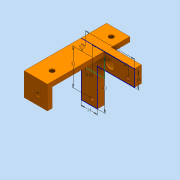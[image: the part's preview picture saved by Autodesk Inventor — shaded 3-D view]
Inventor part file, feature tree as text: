
AUTODESK INVENTOR PART (.ipt)
format: ipt  version: 2016 (Build 200138000, 138)  size: 232,448 bytes
history: native  units: mm
features: extrude x9, sketch x9, hole x7
ambient origin geometry x8: Origin, YZ Plane, XZ Plane, XY Plane, X Axis, Y Axis, Z Axis, Center Point
bodies: Solid1 (feature_tree)
feature tree (25):
  extrude  "Extrusion1"  Depth=20.0mm
  extrude  "Extrusion2"  Depth=45.0mm TaperAngle=0.0deg
  hole  "Hole2"  [1 undecoded]
  hole  "Hole3"  [1 undecoded]
  hole  "Hole4"  [1 undecoded]
  sketch  "Sketch3"  dims[d15=37.0mm d16=8.0mm d17=4.0mm d18=6.0mm d19=8.0mm d20=2.0mm d21=90.0deg d22=8.0mm d23=20.594885mm]
  sketch  "Sketch4"  dims[d24=37.0mm d25=8.0mm d26=4.0mm d27=6.0mm d28=8.0mm d29=2.0mm d30=90.0deg d31=8.0mm d32=20.594885mm]
  sketch  "Sketch5"  dims[d33=8.0mm d34=8.0mm d35=4.0mm d36=6.0mm d37=8.0mm d38=2.0mm d39=90.0deg d40=8.0mm d41=20.594885mm d51=7.0mm]
  extrude  "Extrusion3"  Depth=14.0mm
  extrude  "Extrusion4"  Depth=42.0mm
  extrude  "Extrusion5"  Depth=5.5mm
  sketch  "Sketch6"  dims[d52=7.0mm d53=7.0mm]
  extrude  "Extrusion6"  Depth=5.5mm
  hole  "Hole5"  [1 undecoded]
  extrude  "Extrusion7"  Depth=2.0mm
  hole  "Hole6"  [1 undecoded]
  hole  "Hole7"  [1 undecoded]
  sketch  "Sketch8"  dims[d58=3.2mm d59=0.0mm d62=14.0mm]
  extrude  "Extrusion8"  Depth=20.0mm
  extrude  "Extrusion9"  Depth=4.0mm
  hole  "Hole8"  [1 undecoded]
  sketch  "Sketch1"  dims[d0=20.0mm d1=20.0mm]
  sketch  "Sketch2"  dims[d2=4.0mm d3=0.0mm d4=45.0mm d5=0.0mm]
  sketch  "Sketch7"  dims[d54=3.2mm d55=0.0mm d56=3.2mm d57=0.0mm]
  sketch  "Sketch9"  dims[d65=42.0mm d66=42.0mm d68=5.5mm d69=5.5mm d70=31.0mm d71=31.0mm d72=14.0mm d73=6.0mm d74=0.0mm d75=3.0mm d76=6.0mm d77=4.0mm d78=2.0mm d79=90.0deg d80=8.0mm d81=20.594885mm d82=20.0mm d83=4.0mm d84=4.0mm d85=20.0mm d86=16.0mm d87=0.0mm d88=8.0mm d89=8.0mm d90=4.0mm d91=6.0mm d92=4.0mm d93=2.0mm d94=90.0deg d95=8.0mm d96=20.594885mm d97=8.0mm d98=8.0mm d99=4.0mm d100=6.0mm d101=4.0mm d102=2.0mm d103=90.0deg d104=8.0mm d105=20.594885mm d106=7.0mm d107=7.0mm d108=3.2mm d109=0.0mm d110=3.2mm d111=0.0mm d112=25.0mm d113=7.0mm d114=8.0mm d115=6.0mm d116=4.0mm d117=2.0mm d118=90.0deg d119=8.0mm d120=20.594885mm]
note: 7 required parameter values undecoded (feature->parameter linkage not recoverable at this tier; creation-order binding heuristic only, values carry confidence <= 0.55)
